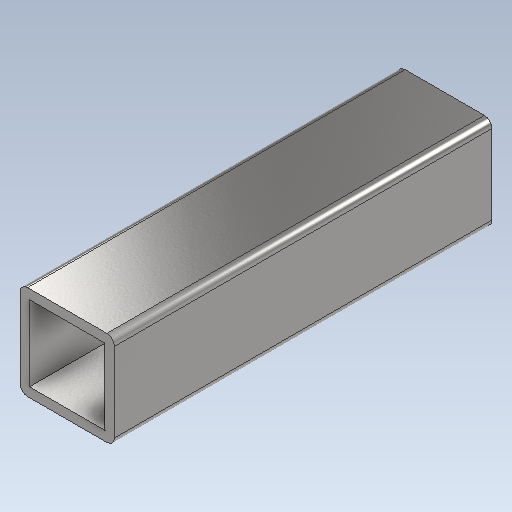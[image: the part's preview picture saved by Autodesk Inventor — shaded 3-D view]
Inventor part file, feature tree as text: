
AUTODESK INVENTOR PART (.ipt)
format: ipt  version: 2021 (Build 250183000, 183)  size: 187,904 bytes
history: native  units: mm
features: extrude x1, fillet x1, plane x1, split x1, other x1, sketch x1
ambient origin geometry x8: Origin, YZ Plane, XZ Plane, XY Plane, X Axis, Y Axis, Z Axis, Center Point
bodies: Solid1 (feature_tree)
feature tree (6):
  extrude  "Extrusion1"  Depth=25.0mm
  fillet  "Fillet1"  Radius=12.5mm
  plane  "Work Plane1"
  split  "Split1"
  other  "axialPlane"
  sketch  "Sketch1"  dims[d0=25.0mm d1=25.0mm d2=12.5mm d3=12.5mm d4=2.5mm d5=1000.0mm d6=0.0mm d7=2.0mm d8=-100.0mm]
